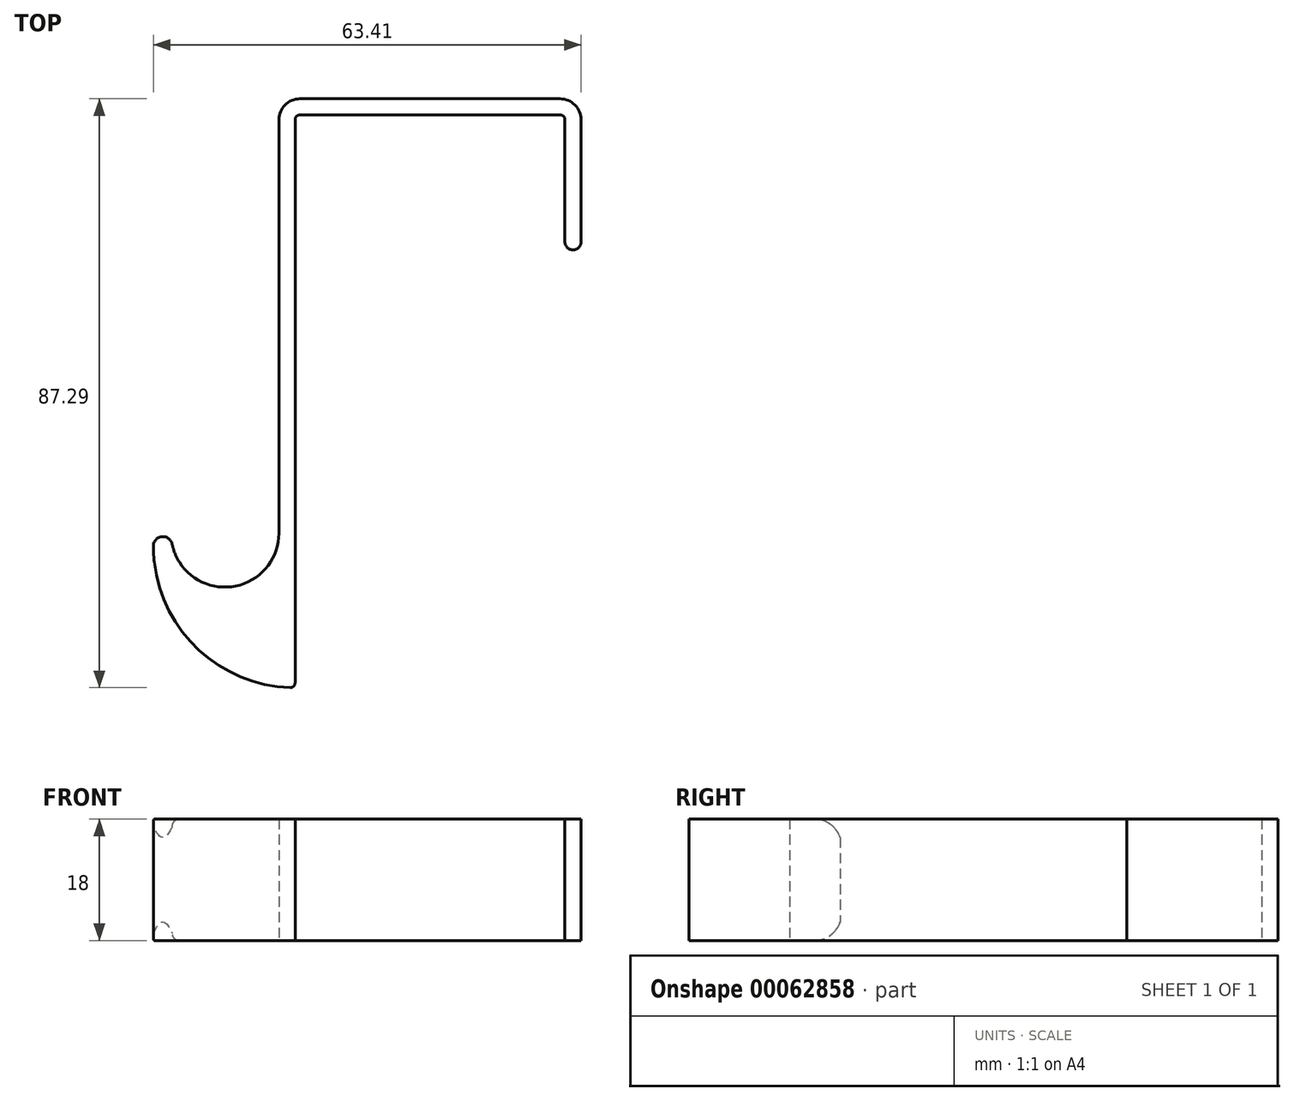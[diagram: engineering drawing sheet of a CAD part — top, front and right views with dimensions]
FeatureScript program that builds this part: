
annotation { "Feature Type Name" : "Feature", "Feature Type Description" : "" }
export const myFeature = defineFeature(function(context is Context, id is Id, definition is map)
    precondition{}
    {
        {
            var Q0;
            Q0=qCreatedBy(makeId("Top.planeOp"),FACE);
            var sketch = newSketch(context, id + "F0", { "sketchPlane" : qUnion([Q0])});
            skLineSegment(sketch, "E0", {"start": v(44.8, -21.2) * mm, "end": v(44.8, -3.1) * mm});
            skLineSegment(sketch, "E1", {"start": v(41.7, 0) * mm, "end": v(3.1, 0) * mm});
            skLineSegment(sketch, "E2", {"start": v(0, -3.1) * mm, "end": v(0, -64.4) * mm});
            skArc(sketch, "E3", {"start": v(-15.83, -66.02) * mm, "mid": v(-7.19, -72.36) * mm, "end": v(0, -64.4) * mm});
            skLineSegment(sketch, "E4", {"start": v(-15.83, -66.02) * mm, "end": v(-8, -64.4) * mm, "construction": true});
            skLineSegment(sketch, "E5", {"start": v(-8, -64.4) * mm, "end": v(0, -64.4) * mm, "construction": true});
            skArc(sketch, "E6", {"start": v(-15.83, -66.02) * mm, "mid": v(-17.35, -64.9) * mm, "end": v(-18.6, -66.3) * mm});
            skArc(sketch, "E7", {"start": v(-18.6, -66.3) * mm, "mid": v(-12.7, -80.9) * mm, "end": v(1.68, -87.3) * mm});
            skLineSegment(sketch, "E8", {"start": v(2.4, -86.6) * mm, "end": v(2.4, -3.1) * mm});
            skLineSegment(sketch, "E9", {"start": v(3.1, -2.4) * mm, "end": v(41.7, -2.4) * mm});
            skLineSegment(sketch, "E10", {"start": v(42.4, -3.1) * mm, "end": v(42.4, -21.2) * mm});
            skArc(sketch, "E11", {"start": v(42.4, -21.2) * mm, "mid": v(43.6, -22.4) * mm, "end": v(44.8, -21.2) * mm});
            skPoint(sketch, "E12.visualSharp", {"position": v(2.4, -2.4) * mm});
            skArc(sketch, "E12.filletArc", {"start": v(3.1, -2.4) * mm, "mid": v(2.6, -2.6) * mm, "end": v(2.4, -3.1) * mm});
            skPoint(sketch, "E13.visualSharp", {"position": v(42.4, -2.4) * mm});
            skArc(sketch, "E13.filletArc", {"start": v(42.4, -3.1) * mm, "mid": v(42.2, -2.6) * mm, "end": v(41.7, -2.4) * mm});
            skPoint(sketch, "E14.visualSharp", {"position": v(44.8, 0) * mm});
            skArc(sketch, "E14.filletArc", {"start": v(44.8, -3.1) * mm, "mid": v(43.9, -0.9) * mm, "end": v(41.7, 0) * mm});
            skPoint(sketch, "E15.visualSharp", {"position": v(0, 0) * mm});
            skArc(sketch, "E15.filletArc", {"start": v(3.1, 0) * mm, "mid": v(0.9, -0.9) * mm, "end": v(0, -3.1) * mm});
            skLineSegment(sketch, "E16", {"start": v(-18.6, -66.3) * mm, "end": v(-18.6, -64.4) * mm, "construction": true});
            skLineSegment(sketch, "E17", {"start": v(-18.6, -64.4) * mm, "end": v(-8, -64.4) * mm, "construction": true});
            skPoint(sketch, "E18.visualSharp", {"position": v(2.4, -87.3) * mm});
            skArc(sketch, "E18.filletArc", {"start": v(1.68, -87.3) * mm, "mid": v(2.19, -87.1) * mm, "end": v(2.4, -86.6) * mm});
            skLineSegment(sketch, "E19", {"start": v(-18.6, -64.9) * mm, "end": v(-15.83, -64.9) * mm, "construction": true});
            skLineSegment(sketch, "E20", {"start": v(-15.83, -64.9) * mm, "end": v(-15.83, -66.02) * mm, "construction": true});
            skSolve(sketch);
        }
        {
            var Q0;
            Q0=makeQuery(id+"F0.imprint","IMPRINT",FACE,{"disambiguationData":[TD([[makeQuery(id+"F0.imprint","IMPRINT",EDGE,{"derivedFrom":sQuery(id+"F0.wireOp",EDGE,"E0")}),1.0]])]});
            extrude(context, id + "F1", {"entities" : qUnion([Q0]), "depth" : 18 * mm, "symmetric" : true});
        }
        {
            var Q0;
            Q0=qCreatedBy(makeId("Right.planeOp"),FACE);
            var sketch = newSketch(context, id + "F2", { "sketchPlane" : qUnion([Q0])});
            skArc(sketch, "E21", {"start": v(-68.7, -9) * mm, "mid": v(-65.87, -7.83) * mm, "end": v(-64.7, -5) * mm});
            skLineSegment(sketch, "E22", {"start": v(-64.7, -5) * mm, "end": v(-64.7, 5) * mm});
            skArc(sketch, "E23", {"start": v(-64.7, 5) * mm, "mid": v(-65.87, 7.83) * mm, "end": v(-68.7, 9) * mm});
            skLineSegment(sketch, "E24", {"start": v(-68.7, -9) * mm, "end": v(-68.7, -10) * mm});
            skLineSegment(sketch, "E25", {"start": v(-68.7, -10) * mm, "end": v(-63.7, -10) * mm});
            skLineSegment(sketch, "E26", {"start": v(-63.7, -10) * mm, "end": v(-63.7, 10) * mm});
            skLineSegment(sketch, "E27", {"start": v(-63.7, 10) * mm, "end": v(-68.7, 10) * mm});
            skLineSegment(sketch, "E28", {"start": v(-68.7, 10) * mm, "end": v(-68.7, 9) * mm});
            skLineSegment(sketch, "E29", {"start": v(-68.7, -9) * mm, "end": v(-68.7, 9) * mm, "construction": true});
            skLineSegment(sketch, "E30", {"start": v(-63.7, 0) * mm, "end": v(-68.7, 0) * mm, "construction": true});
            skSolve(sketch);
        }
        {
            var Q0;
            Q0 = qSketchRegion(id + "F2", true);
            extrude(context, id + "F3", {"entities" : qUnion([Q0]), "operationType" : NewBodyOperationType.REMOVE, "flatOperationType" : FlatOperationType.REMOVE, "oppositeDirection" : true, "offsetDistance" : 25 * mm, "depth" : 30 * mm, "hasSecondDirection" : true, "secondDirectionOppositeDirection" : true, "secondDirectionDepth" : 10 * mm, "domain" : OperationDomain.MODEL});
        }
    });
